# Revit family: Drinking_Fountain-Haws_Corporation-Pedestal_3150
name_source: partatom
category: Plumbing Fixtures
revit_build: Autodesk Revit Architecture 2015 (Build: 20140606_1530(x64)
units: mm (PartAtom-declared; Revit-internal decimal feet)

## types (2) — shared parameters
Assembly Code = D2010810
Cost Note = For Cost information please visit the Resource tab in the Product Page URL
Flow = 0.00 GPM
HW Connection = No
Keynote = 15410.A1
Manufacturer = Haws Corporation
Pedestal = Concrete - Haws Corporation - Exposed Aggregate
Product Documentation Link = https://www.hawsco.com
Product Page URL = http://www.hawsco.com
Sanitary Radius = 1/2"
Series = Haws concrete pedestal drinking fountains
Supply Radius = 0"
URL = http://www.hawsco.com
Vent Connection = No
Version = 2014-v2.0a
zero-valued in all types: Cost

## per-type parameters (varying)
| type | Bowl | CWFU | Description | HWFU | Type Comments | WFU |
| 3150 | Metal - Haws Corporation - Polished Chrome - 5703M | 1 | The "Hi-Lo" adult or child barrier free design of the 3150 allows the square pedestal to be placed securely in multiple locations | 1 | Without freeze-resistant valve assembly | 1 |
| 3150FR | Metal - Haws Corporation - Stainless Steel - With Bead | 2 | The "Hi-Lo" adult or child barrier free design of the 3150FR allows the square pedestal to be placed securely in multiple locations | 2 | Use a freeze-resistant valve assembly to provide year round operation | 2 |

note: column(s) folded — value = type name in every type: Model

## geometry (parser evidence)
native form markers: Blend x36, Sweep x4
no freeform markers — native parametric forms only
